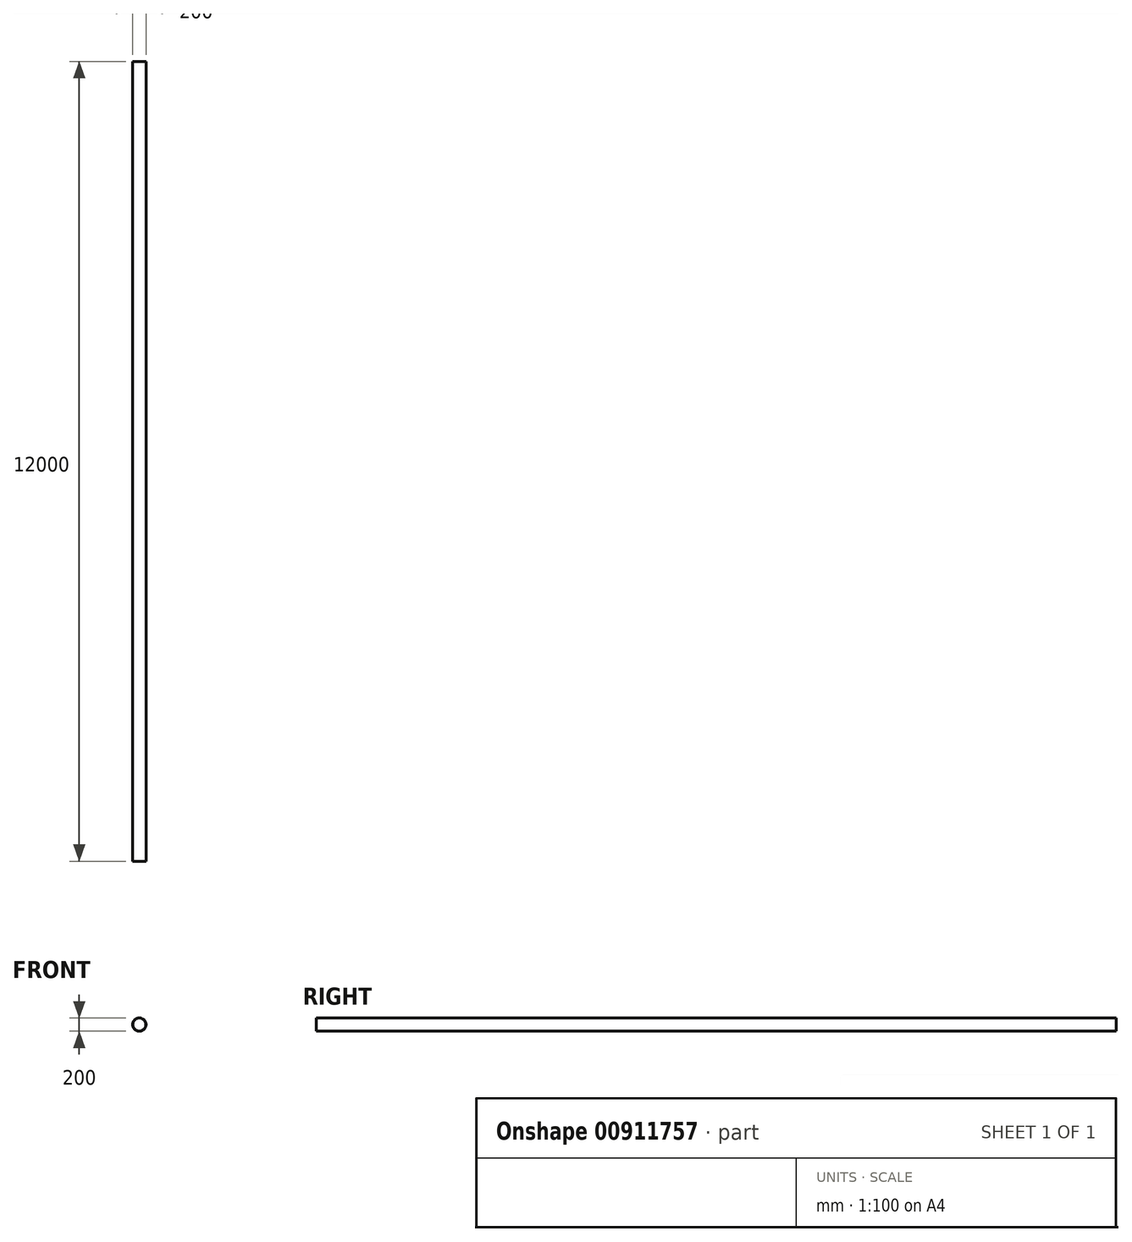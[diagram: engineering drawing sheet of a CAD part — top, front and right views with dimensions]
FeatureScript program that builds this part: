
annotation { "Feature Type Name" : "Feature", "Feature Type Description" : "" }
export const myFeature = defineFeature(function(context is Context, id is Id, definition is map)
    precondition{}
    {
        {
            var Q0;
            Q0=qCreatedBy(makeId("Front.planeOp"),FACE);
            var sketch = newSketch(context, id + "F0", { "sketchPlane" : qUnion([Q0])});
            skCircle(sketch, "E0", {"center": v(0, 0) * mm, "radius": 100 * mm});
            skCircle(sketch, "E1", {"center": v(0, 0) * mm, "radius": 98 * mm});
            skSolve(sketch);
        }
        {
            var Q0;
            Q0=sQuery(id+"F0.wireOp",EDGE,"E0");
            var Q1;
            Q1=sQuery(id+"F0.wireOp",EDGE,"E1");
            extrude(context, id + "F1", {"bodyType" : ToolBodyType.SURFACE, "surfaceEntities" : qUnion([Q0, Q1]), "depth" : 12000 * mm, "offsetDistance" : 25 * mm});
        }
    });
